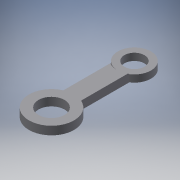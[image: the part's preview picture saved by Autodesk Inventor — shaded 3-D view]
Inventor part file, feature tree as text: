
AUTODESK INVENTOR PART (.ipt)
format: ipt  version: 2016 (Build 200138000, 138)  size: 121,344 bytes
history: native  units: mm
features: extrude x2, sketch x2, chamfer x1
ambient origin geometry x8: Origin, YZ Plane, XZ Plane, XY Plane, X Axis, Y Axis, Z Axis, Center Point
bodies: Solid1 (feature_tree)
feature tree (5):
  extrude  "Extrusion1"  Depth=17.0mm
  extrude  "Extrusion2"  Depth=65.0mm
  chamfer  "Chamfer1"  Distance=8.0mm
  sketch  "Sketch1"  dims[d0=22.0mm d1=17.0mm]
  sketch  "Sketch2"  dims[d2=65.0mm d3=5.5mm d4=8.0mm d5=15.0mm d6=7.0mm d7=0.0mm d8=1.0mm d9=0.0mm d10=1.0mm d11=2.0mm d12=45.0deg]
